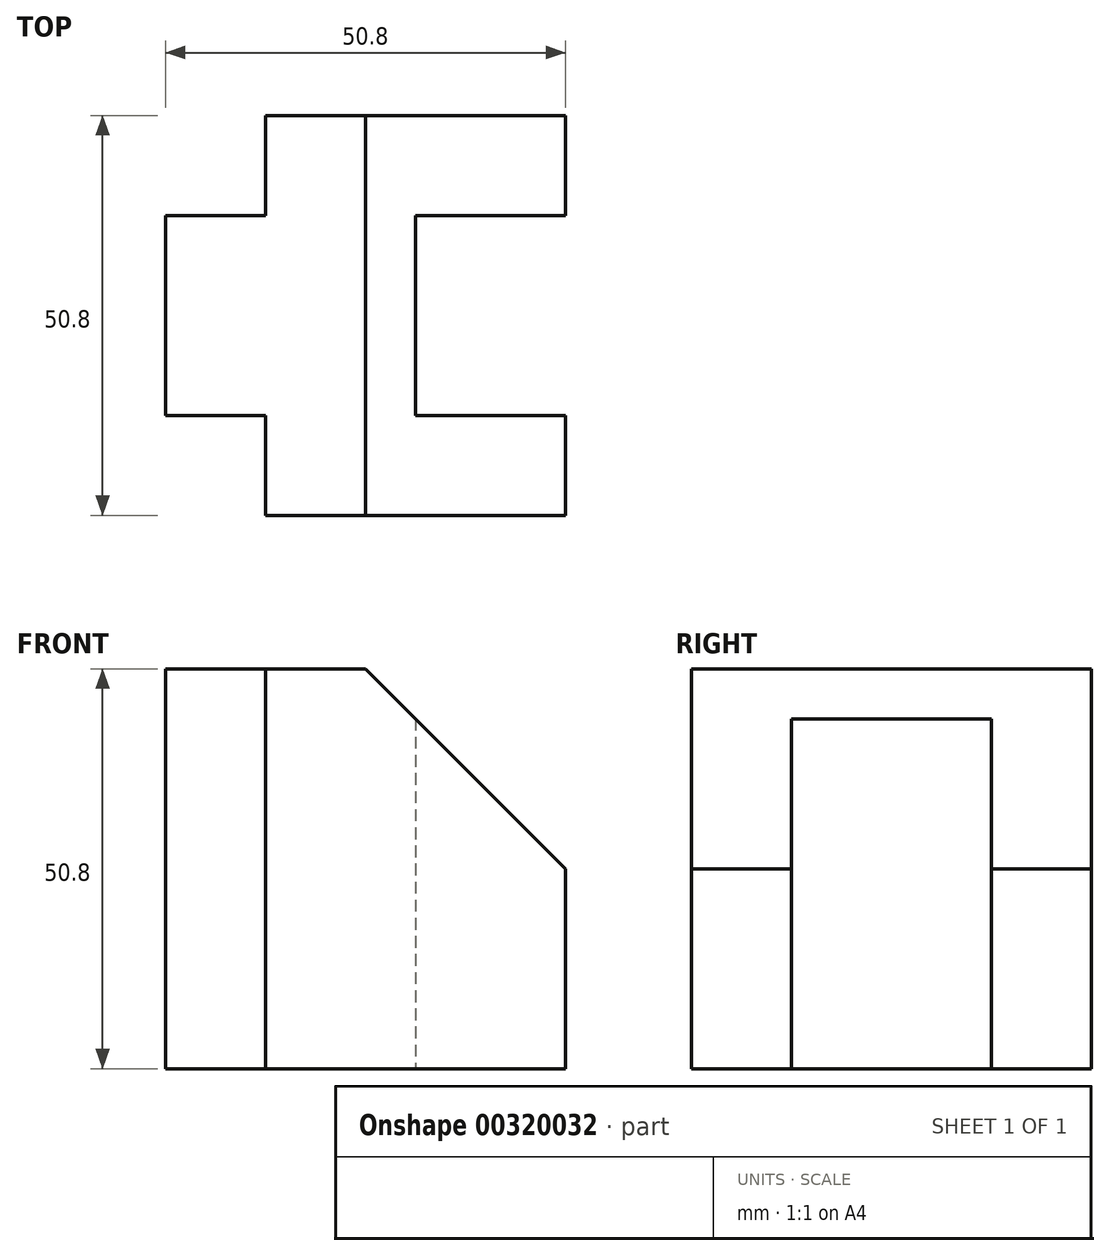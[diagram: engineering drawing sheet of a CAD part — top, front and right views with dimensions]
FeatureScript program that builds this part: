
annotation { "Feature Type Name" : "Feature", "Feature Type Description" : "" }
export const myFeature = defineFeature(function(context is Context, id is Id, definition is map)
    precondition{}
    {
        {
            var Q0;
            Q0=qCreatedBy(makeId("Top.planeOp"),FACE);
            var sketch = newSketch(context, id + "F0", { "sketchPlane" : qUnion([Q0])});
            skLineSegment(sketch, "E0", {"start": v(0, 0) * mm, "end": v(0, -25.4) * mm});
            skLineSegment(sketch, "E1", {"start": v(0, -25.4) * mm, "end": v(12.7, -25.4) * mm});
            skLineSegment(sketch, "E2", {"start": v(12.7, -25.4) * mm, "end": v(12.7, -38.1) * mm});
            skLineSegment(sketch, "E3", {"start": v(12.7, -38.1) * mm, "end": v(25.4, -38.1) * mm});
            skLineSegment(sketch, "E4", {"start": v(25.4, -38.1) * mm, "end": v(25.4, 12.7) * mm});
            skLineSegment(sketch, "E5", {"start": v(25.4, 12.7) * mm, "end": v(12.7, 12.7) * mm});
            skLineSegment(sketch, "E6", {"start": v(12.7, 12.7) * mm, "end": v(12.7, 0) * mm});
            skLineSegment(sketch, "E7", {"start": v(12.7, 0) * mm, "end": v(0, 0) * mm});
            skSolve(sketch);
        }
        {
            var Q0;
            Q0 = qSketchRegion(id + "F0", true);
            extrude(context, id + "F1", {"entities" : qUnion([Q0]), "depth" : 50.8 * mm});
        }
        {
            var Q0;
            Q0=makeQuery(id+"F1.opExtrude","SWEPT_FACE",FACE,{"disambiguationData":[OSD([sQuery(id+"F0.wireOp",EDGE,"E3")])]});
            var sketch = newSketch(context, id + "F2", { "sketchPlane" : qUnion([Q0])});
            skLineSegment(sketch, "E8", {"start": v(25.4, 50.8) * mm, "end": v(25.4, 0) * mm});
            skLineSegment(sketch, "E9", {"start": v(25.4, 0) * mm, "end": v(50.8, 0) * mm});
            skLineSegment(sketch, "E10", {"start": v(50.8, 0) * mm, "end": v(50.8, 25.4) * mm});
            skLineSegment(sketch, "E11", {"start": v(50.8, 25.4) * mm, "end": v(25.4, 50.8) * mm});
            skSolve(sketch);
        }
        {
            var Q0;
            Q0 = qSketchRegion(id + "F2", true);
            extrude(context, id + "F3", {"entities" : qUnion([Q0]), "operationType" : NewBodyOperationType.ADD, "oppositeDirection" : true, "depth" : 50.8 * mm});
        }
        {
            var Q0;
            Q0=makeQuery(id+"F3.boolean.opBoolean","MERGE",FACE,{"derivedFrom":[makeQuery(id+"F1.opExtrude","CAP_FACE",FACE,{"disambiguationData":[OSD([sQuery(id+"F0.wireOp",EDGE,"E0"),sQuery(id+"F0.wireOp",EDGE,"E1"),sQuery(id+"F0.wireOp",EDGE,"E2"),sQuery(id+"F0.wireOp",EDGE,"E3"),sQuery(id+"F0.wireOp",EDGE,"E4"),sQuery(id+"F0.wireOp",EDGE,"E5"),sQuery(id+"F0.wireOp",EDGE,"E6"),sQuery(id+"F0.wireOp",EDGE,"E7")])],"isStart":true}),makeQuery(id+"F3.opExtrude","SWEPT_FACE",FACE,{"disambiguationData":[OSD([sQuery(id+"F2.wireOp",EDGE,"E9")])]})]});
            var sketch = newSketch(context, id + "F4", { "sketchPlane" : qUnion([Q0])});
            skLineSegment(sketch, "E12", {"start": v(50.8, 25.4) * mm, "end": v(31.75, 25.4) * mm});
            skLineSegment(sketch, "E13", {"start": v(31.75, 25.4) * mm, "end": v(31.75, 0) * mm});
            skLineSegment(sketch, "E14", {"start": v(31.75, 0) * mm, "end": v(50.8, 0) * mm});
            skLineSegment(sketch, "E15", {"start": v(50.8, 25.4) * mm, "end": v(50.8, 0) * mm});
            skSolve(sketch);
        }
        {
            var Q0;
            Q0 = qSketchRegion(id + "F4", true);
            extrude(context, id + "F5", {"entities" : qUnion([Q0]), "operationType" : NewBodyOperationType.REMOVE, "oppositeDirection" : true, "depth" : 50.8 * mm});
        }
    });
